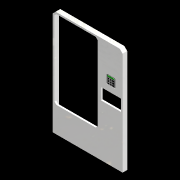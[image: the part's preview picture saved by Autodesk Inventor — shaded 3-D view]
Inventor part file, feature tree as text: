
AUTODESK INVENTOR PART (.ipt)
format: ipt  version: 2020 (Build 240168000, 168)  size: 225,280 bytes
history: native  units: mm
features: other x5, chamfer x1, extrude x1, sketch x1
ambient origin geometry x8: Origin, YZ Plane, XZ Plane, XY Plane, X Axis, Y Axis, Z Axis, Center Point
bodies: Body1 (feature_tree)
feature tree (8):
  other  "自動販賣機.ipt"
  chamfer  "倒角1"  Distance=10.0mm
  extrude  "擠出1"  Depth=50.0mm TaperAngle=45.0deg
  other  "實體2::自動販賣機.ipt"
  other  "標籤特徵1"
  sketch  "草圖1"
  other  "實體1"
  other  "投影切割邊1"
